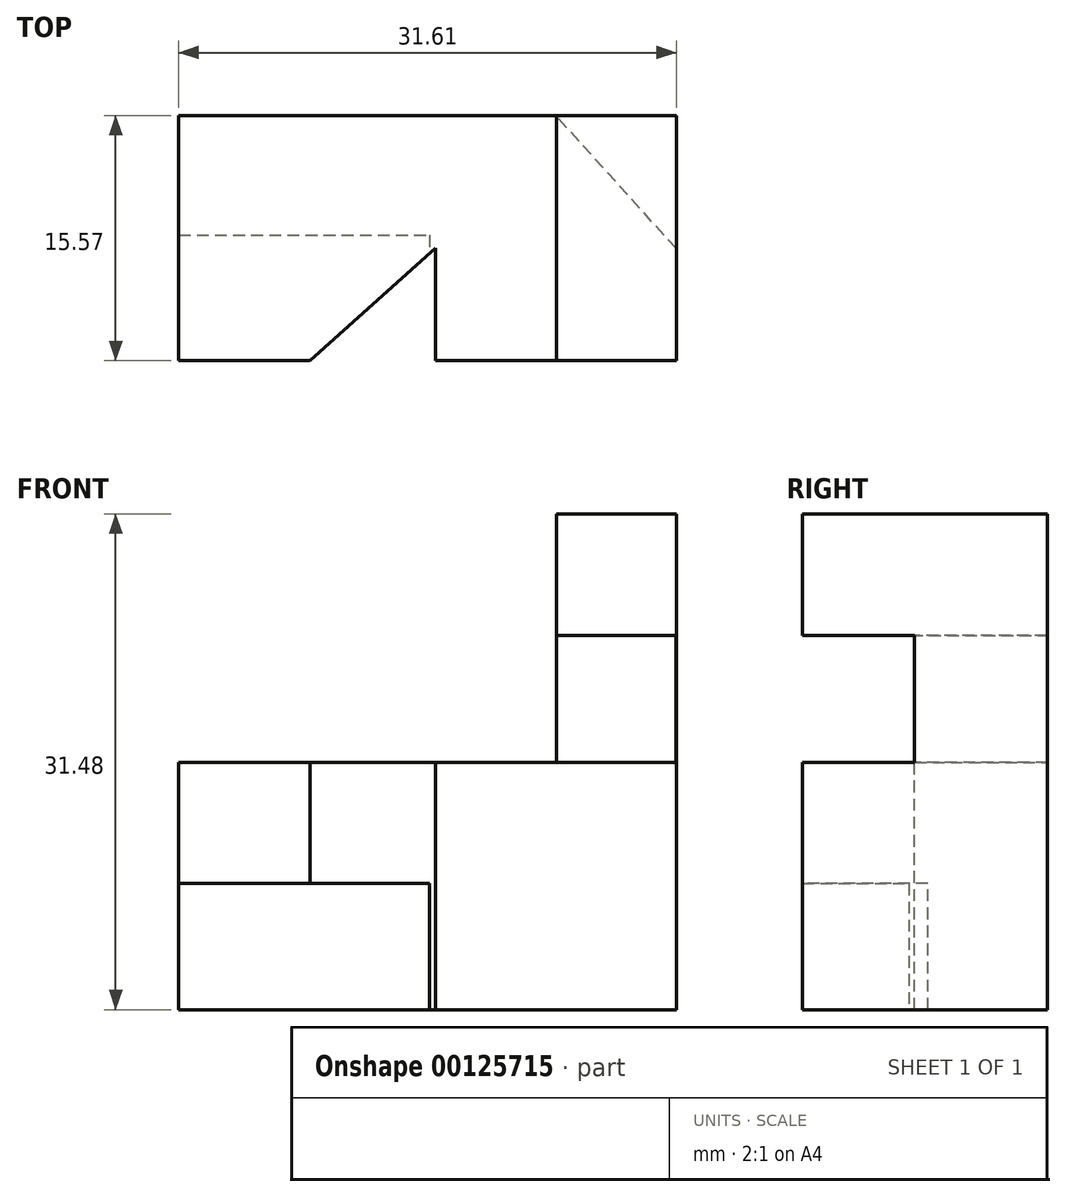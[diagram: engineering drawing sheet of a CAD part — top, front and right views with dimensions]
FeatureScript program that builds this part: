
annotation { "Feature Type Name" : "Feature", "Feature Type Description" : "" }
export const myFeature = defineFeature(function(context is Context, id is Id, definition is map)
    precondition{}
    {
        {
            var Q0;
            Q0=qCreatedBy(makeId("Top.planeOp"),FACE);
            var sketch = newSketch(context, id + "F0", { "sketchPlane" : qUnion([Q0])});
            skLineSegment(sketch, "E0.bottom", {"start": v(-16.32, 8.44) * mm, "end": v(15.3, 8.44) * mm});
            skLineSegment(sketch, "E0.top", {"start": v(-16.32, -7.13) * mm, "end": v(15.3, -7.13) * mm});
            skLineSegment(sketch, "E0.left", {"start": v(-16.32, 8.44) * mm, "end": v(-16.32, -7.13) * mm});
            skLineSegment(sketch, "E0.right", {"start": v(15.3, 8.44) * mm, "end": v(15.3, -7.13) * mm});
            skSolve(sketch);
        }
        {
            var Q0;
            Q0=makeQuery(id+"F0.imprint","IMPRINT",FACE,{"disambiguationData":[TD([[makeQuery(id+"F0.imprint","IMPRINT",EDGE,{"derivedFrom":sQuery(id+"F0.wireOp",EDGE,"E0.bottom")}),-1.0]])]});
            extrude(context, id + "F1", {"entities" : qUnion([Q0]), "depth" : 15.71 * mm});
        }
        {
            var Q0;
            Q0=makeQuery(id+"F1.opExtrude","SWEPT_FACE",FACE,{"disambiguationData":[OSD([sQuery(id+"F0.wireOp",EDGE,"E0.top")])]});
            var sketch = newSketch(context, id + "F2", { "sketchPlane" : qUnion([Q0])});
            skLineSegment(sketch, "E1.bottom", {"start": v(15.3, 15.71) * mm, "end": v(7.66, 15.71) * mm});
            skLineSegment(sketch, "E1.top", {"start": v(15.3, 31.48) * mm, "end": v(7.66, 31.48) * mm});
            skLineSegment(sketch, "E1.left", {"start": v(15.3, 15.71) * mm, "end": v(15.3, 31.48) * mm});
            skLineSegment(sketch, "E1.right", {"start": v(7.66, 15.71) * mm, "end": v(7.66, 31.48) * mm});
            skSolve(sketch);
        }
        {
            var Q0;
            Q0=makeQuery(id+"F2.imprint","IMPRINT",FACE,{"disambiguationData":[TD([[makeQuery(id+"F2.imprint","IMPRINT",EDGE,{"derivedFrom":sQuery(id+"F2.wireOp",EDGE,"E1.bottom")}),1.0]])]});
            extrude(context, id + "F3", {"entities" : qUnion([Q0]), "operationType" : NewBodyOperationType.ADD, "oppositeDirection" : true, "depth" : 15.55 * mm});
        }
        {
            var Q0;
            Q0=makeQuery(id+"F3.boolean.opBoolean","MERGE",FACE,{"derivedFrom":[makeQuery(id+"F1.opExtrude","SWEPT_FACE",FACE,{"disambiguationData":[OSD([sQuery(id+"F0.wireOp",EDGE,"E0.top")])]}),makeQuery(id+"F3.opExtrude","CAP_FACE",FACE,{"disambiguationData":[OSD([sQuery(id+"F2.wireOp",EDGE,"E1.bottom"),sQuery(id+"F2.wireOp",EDGE,"E1.top"),sQuery(id+"F2.wireOp",EDGE,"E1.left"),sQuery(id+"F2.wireOp",EDGE,"E1.right")])],"isStart":true})]});
            var sketch = newSketch(context, id + "F4", { "sketchPlane" : qUnion([Q0])});
            skLineSegment(sketch, "E2", {"start": v(7.66, 23.83) * mm, "end": v(15.3, 23.83) * mm});
            skLineSegment(sketch, "E3", {"start": v(-0.4, 0) * mm, "end": v(-0.4, 15.71) * mm});
            skLineSegment(sketch, "E4", {"start": v(7.66, 15.71) * mm, "end": v(15.3, 15.71) * mm});
            skLineSegment(sketch, "E5", {"start": v(-0.4, 8.01) * mm, "end": v(-16.32, 8.01) * mm});
            skPoint(sketch, "E5.endSnap0", {"position": v(-16.32, 7.86) * mm});
            skLineSegment(sketch, "E6", {"start": v(-8.07, 8.01) * mm, "end": v(-8.07, 15.71) * mm});
            skSolve(sketch);
        }
        {
            var Q0;
            {var subQ4=sQuery(id+"F4.wireOp",EDGE,"E5");Q0=makeQuery(id+"F4.imprint","IMPRINT",FACE,{"disambiguationData":[TD([[makeQuery(id+"F4.imprint","IMPRINT",EDGE,{"derivedFrom":subQ4}),1.0]])]});}
            extrude(context, id + "F5", {"entities" : qUnion([Q0]), "operationType" : NewBodyOperationType.REMOVE, "oppositeDirection" : true, "depth" : 7.97 * mm});
        }
        {
            var Q0;
            Q0=makeQuery(id+"F1.opExtrude","CAP_FACE",FACE,{"disambiguationData":[OSD([sQuery(id+"F0.wireOp",EDGE,"E0.bottom"),sQuery(id+"F0.wireOp",EDGE,"E0.top"),sQuery(id+"F0.wireOp",EDGE,"E0.left"),sQuery(id+"F0.wireOp",EDGE,"E0.right")])],"isStart":false});
            var sketch = newSketch(context, id + "F6", { "sketchPlane" : qUnion([Q0])});
            skLineSegment(sketch, "E7", {"start": v(-7.98, -7.13) * mm, "end": v(0, 0) * mm});
            skLineSegment(sketch, "E8", {"start": v(0, 0) * mm, "end": v(0, -7.13) * mm});
            skLineSegment(sketch, "E9", {"start": v(0, -7.13) * mm, "end": v(-7.98, -7.13) * mm});
            skSolve(sketch);
        }
        {
            var Q0;
            Q0=makeQuery(id+"F6.imprint","IMPRINT",FACE,{"disambiguationData":[TD([[makeQuery(id+"F6.imprint","IMPRINT",EDGE,{"derivedFrom":sQuery(id+"F6.wireOp",EDGE,"E7")}),-1.0]])]});
            extrude(context, id + "F7", {"entities" : qUnion([Q0]), "operationType" : NewBodyOperationType.REMOVE, "oppositeDirection" : true, "depth" : 25 * mm});
        }
        {
            var Q0;
            Q0=makeQuery(id+"F3.boolean.opBoolean","MERGE",FACE,{"derivedFrom":[makeQuery(id+"F1.opExtrude","SWEPT_FACE",FACE,{"disambiguationData":[OSD([sQuery(id+"F0.wireOp",EDGE,"E0.right")])]}),makeQuery(id+"F3.opExtrude","SWEPT_FACE",FACE,{"disambiguationData":[OSD([sQuery(id+"F2.wireOp",EDGE,"E1.left")])]})]});
            var sketch = newSketch(context, id + "F8", { "sketchPlane" : qUnion([Q0])});
            skLineSegment(sketch, "E10", {"start": v(-7.13, 15.71) * mm, "end": v(0, 15.71) * mm});
            skLineSegment(sketch, "E11", {"start": v(-7.13, 23.77) * mm, "end": v(0, 23.77) * mm});
            skLineSegment(sketch, "E12", {"start": v(0, 23.77) * mm, "end": v(0, 15.71) * mm});
            skLineSegment(sketch, "E13", {"start": v(-7.13, 15.71) * mm, "end": v(-7.13, 23.77) * mm});
            skSolve(sketch);
        }
        {
            var Q0;
            Q0=makeQuery(id+"F8.imprint","IMPRINT",FACE,{"disambiguationData":[TD([[makeQuery(id+"F8.imprint","IMPRINT",EDGE,{"derivedFrom":sQuery(id+"F8.wireOp",EDGE,"E10")}),1.0]])]});
            extrude(context, id + "F9", {"entities" : qUnion([Q0]), "operationType" : NewBodyOperationType.REMOVE, "oppositeDirection" : true, "depth" : 25 * mm});
        }
        {
            var Q0;
            Q0=makeQuery(id+"F9.boolean.opBoolean","INTERSECT",EDGE,{"derivedFrom":[makeQuery(id+"F3.opExtrude","SWEPT_FACE",FACE,{"disambiguationData":[OSD([sQuery(id+"F2.wireOp",EDGE,"E1.right")])]}),makeQuery(id+"F9.opExtrude","SWEPT_FACE",FACE,{"disambiguationData":[OSD([sQuery(id+"F8.wireOp",EDGE,"E12")])]})]});
            chamfer(context, id + "F10", {"entities" : qUnion([Q0]), "chamferType" : ChamferType.TWO_OFFSETS, "width1" : 7.6 * mm, "oppositeDirection" : false, "width2" : 8.4 * mm, "tangentPropagation" : true});
        }
    });
